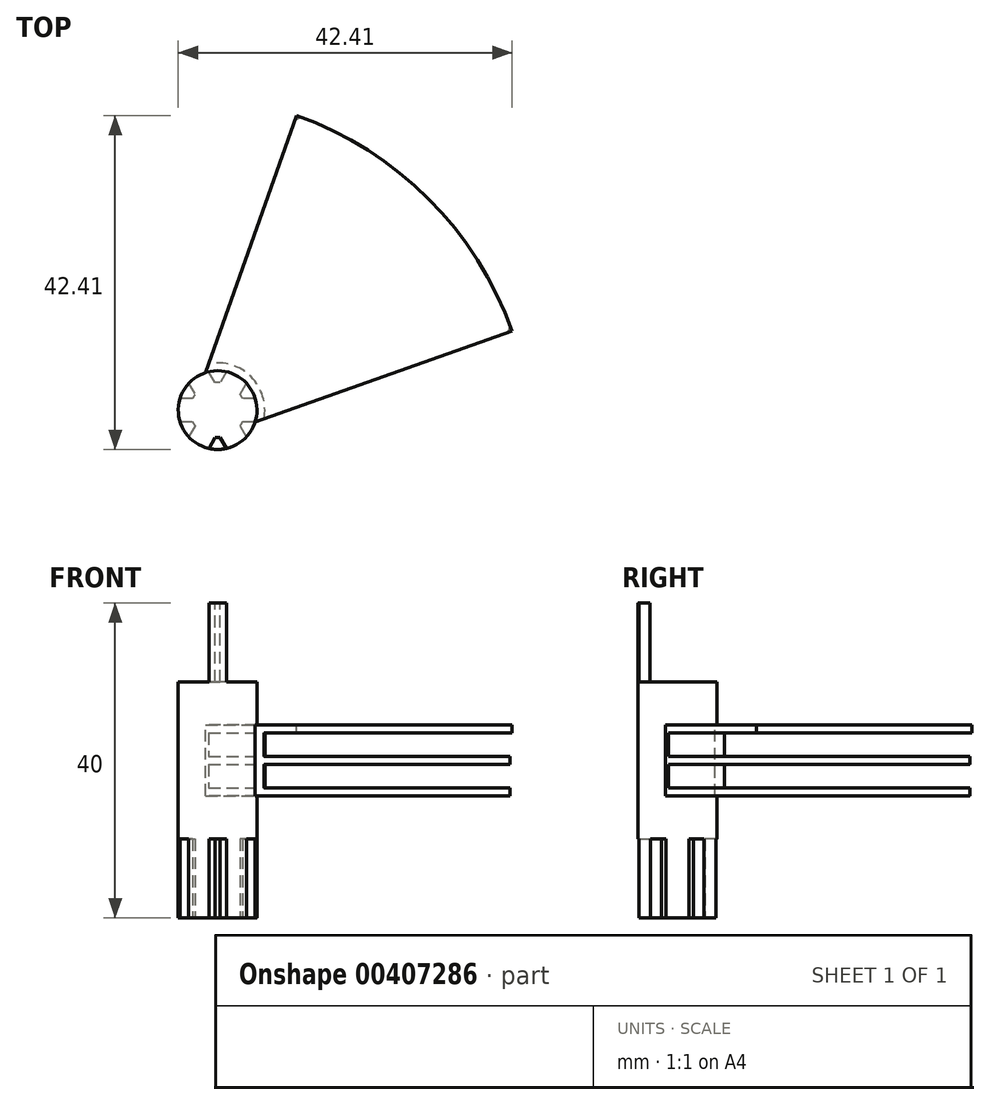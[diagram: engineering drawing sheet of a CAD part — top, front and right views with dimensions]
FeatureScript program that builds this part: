
annotation { "Feature Type Name" : "Feature", "Feature Type Description" : "" }
export const myFeature = defineFeature(function(context is Context, id is Id, definition is map)
    precondition{}
    {
        {
            var Q0;
            Q0=qCreatedBy(makeId("Top.planeOp"),FACE);
            var sketch = newSketch(context, id + "F0", { "sketchPlane" : qUnion([Q0])});
            skCircle(sketch, "E0", {"center": v(0, 0) * mm, "radius": 5 * mm});
            skSolve(sketch);
        }
        {
            var Q0;
            Q0 = qSketchRegion(id + "F0", true);
            extrude(context, id + "F1", {"entities" : qUnion([Q0]), "endBound" : BoundingType.SYMMETRIC, "depth" : 40 * mm});
        }
        {
            var Q0;
            Q0=qCreatedBy(makeId("Top.planeOp"),FACE);
            var sketch = newSketch(context, id + "F2", { "sketchPlane" : qUnion([Q0])});
            skCircle(sketch, "E1", {"center": v(0, 0) * mm, "radius": 40 * mm, "construction": true});
            skCircle(sketch, "E2.0", {"center": v(0, 0) * mm, "radius": 5 * mm});
            skLineSegment(sketch, "E3", {"start": v(0, 0) * mm, "end": v(-5, 0) * mm, "construction": true});
            skLineSegment(sketch, "E4", {"start": v(0, 0) * mm, "end": v(0, -5) * mm, "construction": true});
            skLineSegment(sketch, "E5", {"start": v(0, -5) * mm, "end": v(-6.33, -5) * mm, "construction": true});
            skLineSegment(sketch, "E6", {"start": v(-6.33, -5) * mm, "end": v(-6.33, 0) * mm, "construction": true});
            skLineSegment(sketch, "E7", {"start": v(-6.33, 0) * mm, "end": v(-5, 0) * mm, "construction": true});
            skLineSegment(sketch, "E8", {"start": v(-5, 0) * mm, "end": v(-5, -5) * mm, "construction": true});
            skCircle(sketch, "E9", {"center": v(-5, -5) * mm, "radius": 45 * mm});
            skSolve(sketch);
        }
        {
            var Q0;
            Q0=makeQuery(id+"F2.imprint","IMPRINT",FACE,{"disambiguationData":[TD([[makeQuery(id+"F2.imprint","IMPRINT",EDGE,{"derivedFrom":sQuery(id+"F2.wireOp",EDGE,"E2.0")}),-1.0]])]});
            extrude(context, id + "F3", {"entities" : qUnion([Q0]), "operationType" : NewBodyOperationType.ADD, "endBound" : BoundingType.SYMMETRIC, "depth" : 9 * mm});
        }
        {
            var Q0;
            Q0=qCreatedBy(makeId("Front.planeOp"),FACE);
            var sketch = newSketch(context, id + "F4", { "sketchPlane" : qUnion([Q0])});
            skLineSegment(sketch, "E10", {"start": v(47.5, 3.5) * mm, "end": v(6, 3.5) * mm});
            skLineSegment(sketch, "E11", {"start": v(47.5, 0.5) * mm, "end": v(6, 0.5) * mm});
            skLineSegment(sketch, "E12", {"start": v(47.5, -3.5) * mm, "end": v(6, -3.5) * mm});
            skPoint(sketch, "E13.orphan", {"position": v(-45, -4.5) * mm});
            skPoint(sketch, "E14.orphan", {"position": v(-45, 4.5) * mm});
            skLineSegment(sketch, "E15", {"start": v(47.5, 3.5) * mm, "end": v(47.5, 0.5) * mm});
            skLineSegment(sketch, "E16", {"start": v(47.5, -0.5) * mm, "end": v(47.5, -3.5) * mm});
            skLineSegment(sketch, "E17.trimOffspring", {"start": v(0, 4.5) * mm, "end": v(0, 22.27) * mm, "construction": true});
            skLineSegment(sketch, "E18.trimOffspring", {"start": v(0, -4.5) * mm, "end": v(0, -22.41) * mm, "construction": true});
            skLineSegment(sketch, "E19", {"start": v(-5, 4.5) * mm, "end": v(-5, 20) * mm, "construction": true});
            skLineSegment(sketch, "E20", {"start": v(5, 20) * mm, "end": v(5, 4.5) * mm, "construction": true});
            skLineSegment(sketch, "E21", {"start": v(-5, -20) * mm, "end": v(-5, -4.5) * mm, "construction": true});
            skLineSegment(sketch, "E22", {"start": v(5, -4.5) * mm, "end": v(5, -20) * mm, "construction": true});
            skLineSegment(sketch, "E23", {"start": v(5, 4.5) * mm, "end": v(5, 3.5) * mm, "construction": true});
            skLineSegment(sketch, "E24", {"start": v(47.5, -0.5) * mm, "end": v(6, -0.5) * mm});
            skLineSegment(sketch, "E25", {"start": v(6, -3.5) * mm, "end": v(6, -0.5) * mm});
            skLineSegment(sketch, "E26.trimOffspring", {"start": v(5, 0.5) * mm, "end": v(5, -0.5) * mm, "construction": true});
            skLineSegment(sketch, "E27.trimOffspring", {"start": v(6, 0.5) * mm, "end": v(6, 3.5) * mm});
            skLineSegment(sketch, "E28.trimOffspring", {"start": v(5, -3.5) * mm, "end": v(5, -4.5) * mm, "construction": true});
            skSolve(sketch);
        }
        {
            var Q0;
            Q0=makeQuery(id+"F4.imprint","IMPRINT",FACE,{"disambiguationData":[TD([[makeQuery(id+"F4.imprint","IMPRINT",EDGE,{"derivedFrom":sQuery(id+"F4.wireOp",EDGE,"E12")}),-1.0]])]});
            var Q1;
            Q1=makeQuery(id+"F4.imprint","IMPRINT",FACE,{"disambiguationData":[TD([[makeQuery(id+"F4.imprint","IMPRINT",EDGE,{"derivedFrom":sQuery(id+"F4.wireOp",EDGE,"E10")}),1.0]])]});
            var Q2;
            Q2=sQuery(id+"F4.wireOp",EDGE,"E18.trimOffspring");
            revolve(context, id + "F5", {"operationType" : NewBodyOperationType.REMOVE, "entities" : qUnion([Q0, Q1]), "axis" : qUnion([Q2]), "revolveType" : RevolveType.FULL, "oppositeDirection" : true});
        }
        {
            var Q0;
            Q0=makeQuery(id+"F1.opExtrude","CAP_FACE",FACE,{"disambiguationData":[OSD([sQuery(id+"F0.wireOp",EDGE,"E0")])],"isStart":false});
            var sketch = newSketch(context, id + "F6", { "sketchPlane" : qUnion([Q0])});
            skArc(sketch, "E29.0", {"start": v(-1.54, 4.76) * mm, "mid": v(-3.54, -3.54) * mm, "end": v(4.76, -1.54) * mm, "construction": true});
            skLineSegment(sketch, "E30", {"start": v(-5, -5) * mm, "end": v(-5, 35) * mm, "construction": true});
            skLineSegment(sketch, "E31", {"start": v(-5, -5) * mm, "end": v(35, -5) * mm, "construction": true});
            skLineSegment(sketch, "E32", {"start": v(-5, -5) * mm, "end": v(10.05, 37.4) * mm, "construction": true});
            skLineSegment(sketch, "E33", {"start": v(-0.79, 6.87) * mm, "end": v(10.05, 37.4) * mm});
            skArc(sketch, "E34", {"start": v(10.05, 37.4) * mm, "mid": v(-36.82, -36.82) * mm, "end": v(37.4, 10.05) * mm});
            skPoint(sketch, "E35.MirrorCS.end.orphan", {"position": v(23.28, 23.28) * mm});
            skPoint(sketch, "E35.MirrorCS.start.orphan", {"position": v(33.7, 17.96) * mm});
            skArc(sketch, "E36", {"start": v(-1.54, 4.76) * mm, "mid": v(-3.54, -3.54) * mm, "end": v(4.76, -1.54) * mm});
            skArc(sketch, "E37.trimOffspring", {"start": v(6.22, 1.25) * mm, "mid": v(3.98, 5.63) * mm, "end": v(-0.79, 6.87) * mm, "construction": true});
            skLineSegment(sketch, "E38", {"start": v(-1.54, 4.76) * mm, "end": v(-0.79, 6.87) * mm});
            skArc(sketch, "E39", {"start": v(26.82, 26.82) * mm, "mid": v(19.02, 33.05) * mm, "end": v(10.05, 37.4) * mm});
            skLineSegment(sketch, "E40", {"start": v(-5, -5) * mm, "end": v(26.82, 26.82) * mm, "construction": true});
            skArc(sketch, "E41", {"start": v(26.82, 26.82) * mm, "mid": v(33.05, 19.02) * mm, "end": v(37.4, 10.05) * mm});
            skLineSegment(sketch, "E42", {"start": v(-5, -5) * mm, "end": v(37.4, 10.05) * mm});
            skSolve(sketch);
        }
        {
            var Q0;
            Q0=makeQuery(id+"F6.imprint","IMPRINT",FACE,{"disambiguationData":[TD([[makeQuery(id+"F6.imprint","IMPRINT",EDGE,{"derivedFrom":sQuery(id+"F6.wireOp",EDGE,"E33")}),1.0]])]});
            extrude(context, id + "F7", {"entities" : qUnion([Q0]), "operationType" : NewBodyOperationType.REMOVE, "endBound" : BoundingType.THROUGH_ALL, "oppositeDirection" : true, "depth" : 25 * mm});
        }
        {
            var Q0;
            {var subQ1=sQuery(id+"F6.wireOp",EDGE,"E33");Q0=makeQuery(id+"F7.boolean.opBoolean","COPY",EDGE,{"disambiguationData":[TD([makeQuery(id+"F5.boolean.opBoolean","COPY",FACE,{"derivedFrom":makeQuery(id+"F5.opRevolve","SWEPT_FACE",FACE,{"disambiguationData":[OSD([sQuery(id+"F4.wireOp",EDGE,"E12")])]})})])],"derivedFrom":makeQuery(id+"F7.opExtrude","SWEPT_EDGE",EDGE,{"disambiguationData":[OSD([subQ1,sQuery(id+"F6.wireOp",EDGE,"E34")])]})});}
            var Q1;
            {var subQ0=sQuery(id+"F6.wireOp",EDGE,"E33");Q1=makeQuery(id+"F7.boolean.opBoolean","COPY",EDGE,{"disambiguationData":[TD([makeQuery(id+"F5.boolean.opBoolean","COPY",FACE,{"derivedFrom":makeQuery(id+"F5.opRevolve","SWEPT_FACE",FACE,{"disambiguationData":[OSD([sQuery(id+"F4.wireOp",EDGE,"E11")])]})})])],"derivedFrom":makeQuery(id+"F7.opExtrude","SWEPT_EDGE",EDGE,{"disambiguationData":[OSD([subQ0,sQuery(id+"F6.wireOp",EDGE,"E34")])]})});}
            var Q2;
            {var subQ1=sQuery(id+"F6.wireOp",EDGE,"E33");Q2=makeQuery(id+"F7.boolean.opBoolean","COPY",EDGE,{"disambiguationData":[TD([makeQuery(id+"F5.boolean.opBoolean","COPY",FACE,{"derivedFrom":makeQuery(id+"F5.opRevolve","SWEPT_FACE",FACE,{"disambiguationData":[OSD([sQuery(id+"F4.wireOp",EDGE,"E10")])]})})])],"derivedFrom":makeQuery(id+"F7.opExtrude","SWEPT_EDGE",EDGE,{"disambiguationData":[OSD([subQ1,sQuery(id+"F6.wireOp",EDGE,"E34")])]})});}
            var Q3;
            {var subQ1=sQuery(id+"F6.wireOp",EDGE,"bP0qAmGH-CtDD-ZhHH-eiUR-qPhmpkNQPwfo");Q3=makeQuery(id+"F7.boolean.opBoolean","COPY",EDGE,{"disambiguationData":[TD([makeQuery(id+"F5.boolean.opBoolean","COPY",FACE,{"derivedFrom":makeQuery(id+"F5.opRevolve","SWEPT_FACE",FACE,{"disambiguationData":[OSD([sQuery(id+"F4.wireOp",EDGE,"E12")])]})})])],"derivedFrom":makeQuery(id+"F7.opExtrude","SWEPT_EDGE",EDGE,{"disambiguationData":[OSD([subQ1,sQuery(id+"F6.wireOp",EDGE,"E34")])]})});}
            var Q4;
            {var subQ0=sQuery(id+"F6.wireOp",EDGE,"bP0qAmGH-CtDD-ZhHH-eiUR-qPhmpkNQPwfo");Q4=makeQuery(id+"F7.boolean.opBoolean","COPY",EDGE,{"disambiguationData":[TD([makeQuery(id+"F5.boolean.opBoolean","COPY",FACE,{"derivedFrom":makeQuery(id+"F5.opRevolve","SWEPT_FACE",FACE,{"disambiguationData":[OSD([sQuery(id+"F4.wireOp",EDGE,"E11")])]})})])],"derivedFrom":makeQuery(id+"F7.opExtrude","SWEPT_EDGE",EDGE,{"disambiguationData":[OSD([subQ0,sQuery(id+"F6.wireOp",EDGE,"E34")])]})});}
            var Q5;
            {var subQ1=sQuery(id+"F6.wireOp",EDGE,"bP0qAmGH-CtDD-ZhHH-eiUR-qPhmpkNQPwfo");Q5=makeQuery(id+"F7.boolean.opBoolean","COPY",EDGE,{"disambiguationData":[TD([makeQuery(id+"F5.boolean.opBoolean","COPY",FACE,{"derivedFrom":makeQuery(id+"F5.opRevolve","SWEPT_FACE",FACE,{"disambiguationData":[OSD([sQuery(id+"F4.wireOp",EDGE,"E10")])]})})])],"derivedFrom":makeQuery(id+"F7.opExtrude","SWEPT_EDGE",EDGE,{"disambiguationData":[OSD([subQ1,sQuery(id+"F6.wireOp",EDGE,"E34")])]})});}
            fillet(context, id + "F8", {"entities" : qUnion([Q0, Q1, Q2, Q3, Q4, Q5]), "radius" : 1 * mm, "tangentPropagation" : true, "allowEdgeOverflow" : false});
        }
        {
            var Q0;
            Q0=makeQuery(id+"F1.opExtrude","CAP_FACE",FACE,{"disambiguationData":[OSD([sQuery(id+"F0.wireOp",EDGE,"E0")])],"isStart":false});
            var sketch = newSketch(context, id + "F9", { "sketchPlane" : qUnion([Q0])});
            skCircle(sketch, "E43", {"center": v(0, 0) * mm, "radius": 3.5 * mm, "construction": true});
            skLineSegment(sketch, "E44", {"start": v(0, 0) * mm, "end": v(5, 0) * mm, "construction": true});
            skLineSegment(sketch, "E45", {"start": v(0, 0) * mm, "end": v(-5, 0) * mm, "construction": true});
            skLineSegment(sketch, "E46", {"start": v(0, 0) * mm, "end": v(-2.5, 4.33) * mm, "construction": true});
            skLineSegment(sketch, "E47", {"start": v(0, 0) * mm, "end": v(2.5, 4.33) * mm, "construction": true});
            skLineSegment(sketch, "E48", {"start": v(0, 0) * mm, "end": v(-2.5, -4.33) * mm, "construction": true});
            skLineSegment(sketch, "E49", {"start": v(0, 0) * mm, "end": v(2.5, -4.33) * mm, "construction": true});
            skArc(sketch, "E50", {"start": v(-2.5, 4.33) * mm, "mid": v(-1.82, 4.66) * mm, "end": v(-1.1, 4.88) * mm});
            skArc(sketch, "E51", {"start": v(-2.5, 4.33) * mm, "mid": v(-3.12, 3.9) * mm, "end": v(-3.67, 3.4) * mm});
            skArc(sketch, "E52", {"start": v(2.5, 4.33) * mm, "mid": v(1.82, 4.66) * mm, "end": v(1.1, 4.88) * mm});
            skArc(sketch, "E53", {"start": v(2.5, 4.33) * mm, "mid": v(3.12, 3.9) * mm, "end": v(3.67, 3.4) * mm});
            skArc(sketch, "E54", {"start": v(5, 0) * mm, "mid": v(4.94, 0.75) * mm, "end": v(4.78, 1.48) * mm});
            skArc(sketch, "E55", {"start": v(5, 0) * mm, "mid": v(4.94, -0.75) * mm, "end": v(4.78, -1.48) * mm});
            skArc(sketch, "E56", {"start": v(2.5, -4.33) * mm, "mid": v(1.82, -4.66) * mm, "end": v(1.1, -4.88) * mm});
            skArc(sketch, "E57", {"start": v(2.5, -4.33) * mm, "mid": v(3.12, -3.9) * mm, "end": v(3.67, -3.4) * mm});
            skArc(sketch, "E58", {"start": v(-2.5, -4.33) * mm, "mid": v(-1.82, -4.66) * mm, "end": v(-1.1, -4.88) * mm});
            skArc(sketch, "E59", {"start": v(-2.5, -4.33) * mm, "mid": v(-3.12, -3.9) * mm, "end": v(-3.67, -3.4) * mm});
            skArc(sketch, "E60", {"start": v(-5, 0) * mm, "mid": v(-4.94, -0.75) * mm, "end": v(-4.78, -1.48) * mm});
            skArc(sketch, "E61", {"start": v(-5, 0) * mm, "mid": v(-4.94, 0.75) * mm, "end": v(-4.78, 1.48) * mm});
            skLineSegment(sketch, "E62", {"start": v(-3.67, 3.4) * mm, "end": v(1.1, -4.88) * mm, "construction": true});
            skLineSegment(sketch, "E63", {"start": v(3.67, -3.4) * mm, "end": v(-1.1, 4.88) * mm, "construction": true});
            skLineSegment(sketch, "E64", {"start": v(1.1, 4.88) * mm, "end": v(-3.67, -3.4) * mm, "construction": true});
            skLineSegment(sketch, "E65", {"start": v(-1.1, -4.88) * mm, "end": v(3.67, 3.4) * mm, "construction": true});
            skLineSegment(sketch, "E66", {"start": v(4.78, 1.48) * mm, "end": v(-4.78, 1.48) * mm, "construction": true});
            skLineSegment(sketch, "E67", {"start": v(-4.78, -1.48) * mm, "end": v(4.78, -1.48) * mm, "construction": true});
            skArc(sketch, "E68", {"start": v(-2.87, 2) * mm, "mid": v(-3.03, 1.75) * mm, "end": v(-3.17, 1.48) * mm});
            skArc(sketch, "E69", {"start": v(-3.17, -1.48) * mm, "mid": v(-3.03, -1.75) * mm, "end": v(-2.87, -2) * mm});
            skArc(sketch, "E70", {"start": v(0.3, -3.49) * mm, "mid": v(0, -3.5) * mm, "end": v(-0.3, -3.49) * mm});
            skArc(sketch, "E71", {"start": v(2.87, -2) * mm, "mid": v(3.03, -1.75) * mm, "end": v(3.17, -1.48) * mm});
            skArc(sketch, "E72", {"start": v(3.17, 1.48) * mm, "mid": v(3.03, 1.75) * mm, "end": v(2.87, 2) * mm});
            skArc(sketch, "E73", {"start": v(0.3, 3.49) * mm, "mid": v(0, 3.5) * mm, "end": v(-0.3, 3.49) * mm});
            skLineSegment(sketch, "E74", {"start": v(-1.1, 4.88) * mm, "end": v(-0.3, 3.49) * mm});
            skLineSegment(sketch, "E75", {"start": v(0.3, 3.49) * mm, "end": v(1.1, 4.88) * mm});
            skLineSegment(sketch, "E76", {"start": v(2.87, 2) * mm, "end": v(3.67, 3.4) * mm});
            skLineSegment(sketch, "E77", {"start": v(3.17, 1.48) * mm, "end": v(4.78, 1.48) * mm});
            skLineSegment(sketch, "E78", {"start": v(4.78, -1.48) * mm, "end": v(3.17, -1.48) * mm});
            skLineSegment(sketch, "E79", {"start": v(3.67, -3.4) * mm, "end": v(2.87, -2) * mm});
            skLineSegment(sketch, "E80", {"start": v(1.1, -4.88) * mm, "end": v(0.3, -3.49) * mm});
            skLineSegment(sketch, "E81", {"start": v(-1.1, -4.88) * mm, "end": v(-0.3, -3.49) * mm});
            skLineSegment(sketch, "E82", {"start": v(-3.67, -3.4) * mm, "end": v(-2.87, -2) * mm});
            skLineSegment(sketch, "E83", {"start": v(-4.78, -1.48) * mm, "end": v(-3.17, -1.48) * mm});
            skLineSegment(sketch, "E84", {"start": v(-4.78, 1.48) * mm, "end": v(-3.17, 1.48) * mm});
            skLineSegment(sketch, "E85", {"start": v(-2.87, 2) * mm, "end": v(-3.67, 3.4) * mm});
            skSolve(sketch);
        }
        {
            var Q0;
            Q0=makeQuery(id+"F9.imprint","IMPRINT",FACE,{"disambiguationData":[TD([[makeQuery(id+"F9.imprint","IMPRINT",EDGE,{"derivedFrom":sQuery(id+"F9.wireOp",EDGE,"E68")}),-1.0]])]});
            var Q1;
            Q1=makeQuery(id+"F9.imprint","IMPRINT",FACE,{"disambiguationData":[TD([[makeQuery(id+"F9.imprint","IMPRINT",EDGE,{"derivedFrom":sQuery(id+"F9.wireOp",EDGE,"E73")}),-1.0]])]});
            var Q2;
            Q2=makeQuery(id+"F9.imprint","IMPRINT",FACE,{"disambiguationData":[TD([[makeQuery(id+"F9.imprint","IMPRINT",EDGE,{"derivedFrom":sQuery(id+"F9.wireOp",EDGE,"E72")}),-1.0]])]});
            var Q3;
            Q3=makeQuery(id+"F9.imprint","IMPRINT",FACE,{"disambiguationData":[TD([[makeQuery(id+"F9.imprint","IMPRINT",EDGE,{"derivedFrom":sQuery(id+"F9.wireOp",EDGE,"E71")}),-1.0]])]});
            var Q4;
            Q4=makeQuery(id+"F9.imprint","IMPRINT",FACE,{"disambiguationData":[TD([[makeQuery(id+"F9.imprint","IMPRINT",EDGE,{"derivedFrom":sQuery(id+"F9.wireOp",EDGE,"E70")}),1.0]])]});
            var Q5;
            Q5=makeQuery(id+"F9.imprint","IMPRINT",FACE,{"disambiguationData":[TD([[makeQuery(id+"F9.imprint","IMPRINT",EDGE,{"derivedFrom":sQuery(id+"F9.wireOp",EDGE,"E69")}),-1.0]])]});
            extrude(context, id + "F10", {"entities" : qUnion([Q0, Q1, Q2, Q3, Q4, Q5]), "operationType" : NewBodyOperationType.REMOVE, "oppositeDirection" : true, "depth" : 10 * mm});
        }
        {
            var Q0;
            Q0=makeQuery(id+"F1.opExtrude","CAP_FACE",FACE,{"disambiguationData":[OSD([sQuery(id+"F0.wireOp",EDGE,"E0")])],"isStart":true});
            var sketch = newSketch(context, id + "F11", { "sketchPlane" : qUnion([Q0])});
            skLineSegment(sketch, "E86.0.0", {"start": v(1.1, -4.88) * mm, "end": v(0.3, -3.49) * mm});
            skArc(sketch, "E86.0.1", {"start": v(0.3, -3.49) * mm, "mid": v(0, -3.5) * mm, "end": v(-0.3, -3.49) * mm});
            skLineSegment(sketch, "E86.0.2", {"start": v(-0.3, -3.49) * mm, "end": v(-1.1, -4.88) * mm});
            skArc(sketch, "E86.0.3", {"start": v(-1.1, -4.88) * mm, "mid": v(-2.5, -4.33) * mm, "end": v(-3.67, -3.4) * mm});
            skLineSegment(sketch, "E86.0.4", {"start": v(-3.67, -3.4) * mm, "end": v(-2.87, -2) * mm});
            skArc(sketch, "E86.0.5", {"start": v(-2.87, -2) * mm, "mid": v(-3.03, -1.75) * mm, "end": v(-3.17, -1.48) * mm});
            skLineSegment(sketch, "E86.0.6", {"start": v(-3.17, -1.48) * mm, "end": v(-4.78, -1.48) * mm});
            skArc(sketch, "E86.0.7", {"start": v(-4.78, -1.48) * mm, "mid": v(-5, 0) * mm, "end": v(-4.78, 1.48) * mm});
            skLineSegment(sketch, "E86.0.8", {"start": v(-4.78, 1.48) * mm, "end": v(-3.17, 1.48) * mm});
            skArc(sketch, "E86.0.9", {"start": v(-3.17, 1.48) * mm, "mid": v(-3.03, 1.75) * mm, "end": v(-2.87, 2) * mm});
            skLineSegment(sketch, "E86.0.10", {"start": v(-2.87, 2) * mm, "end": v(-3.67, 3.4) * mm});
            skArc(sketch, "E86.0.11", {"start": v(-3.67, 3.4) * mm, "mid": v(-2.5, 4.33) * mm, "end": v(-1.1, 4.88) * mm});
            skLineSegment(sketch, "E86.0.12", {"start": v(-1.1, 4.88) * mm, "end": v(-0.3, 3.49) * mm});
            skArc(sketch, "E86.0.13", {"start": v(-0.3, 3.49) * mm, "mid": v(0, 3.5) * mm, "end": v(0.3, 3.49) * mm});
            skLineSegment(sketch, "E86.0.14", {"start": v(0.3, 3.49) * mm, "end": v(1.1, 4.88) * mm});
            skArc(sketch, "E86.0.15", {"start": v(1.1, 4.88) * mm, "mid": v(2.5, 4.33) * mm, "end": v(3.67, 3.4) * mm});
            skLineSegment(sketch, "E86.0.16", {"start": v(3.67, 3.4) * mm, "end": v(2.87, 2) * mm});
            skArc(sketch, "E86.0.17", {"start": v(2.87, 2) * mm, "mid": v(3.03, 1.75) * mm, "end": v(3.17, 1.48) * mm});
            skLineSegment(sketch, "E86.0.18", {"start": v(3.17, 1.48) * mm, "end": v(4.78, 1.48) * mm});
            skArc(sketch, "E86.0.19", {"start": v(4.78, 1.48) * mm, "mid": v(5, 0) * mm, "end": v(4.78, -1.48) * mm});
            skLineSegment(sketch, "E86.0.20", {"start": v(4.78, -1.48) * mm, "end": v(3.17, -1.48) * mm});
            skArc(sketch, "E86.0.21", {"start": v(3.17, -1.48) * mm, "mid": v(3.03, -1.75) * mm, "end": v(2.87, -2) * mm});
            skLineSegment(sketch, "E86.0.22", {"start": v(2.87, -2) * mm, "end": v(3.67, -3.4) * mm});
            skArc(sketch, "E86.0.23", {"start": v(3.67, -3.4) * mm, "mid": v(2.5, -4.33) * mm, "end": v(1.1, -4.88) * mm});
            skSolve(sketch);
        }
        {
            var Q0;
            {var subQ0=sQuery(id+"F11.wireOp",EDGE,"E86.0.12");Q0=makeQuery(id+"F11.imprint","IMPRINT",FACE,{"disambiguationData":[TD([[makeQuery(id+"F11.imprint","IMPRINT",EDGE,{"derivedFrom":subQ0}),1.0]])]});}
            var Q1;
            {var subQ0=sQuery(id+"F11.wireOp",EDGE,"E86.0.16");Q1=makeQuery(id+"F11.imprint","IMPRINT",FACE,{"disambiguationData":[TD([[makeQuery(id+"F11.imprint","IMPRINT",EDGE,{"derivedFrom":subQ0}),1.0]])]});}
            var Q2;
            {var subQ0=sQuery(id+"F11.wireOp",EDGE,"E86.0.20");Q2=makeQuery(id+"F11.imprint","IMPRINT",FACE,{"disambiguationData":[TD([[makeQuery(id+"F11.imprint","IMPRINT",EDGE,{"derivedFrom":subQ0}),1.0]])]});}
            var Q3;
            {var subQ0=sQuery(id+"F11.wireOp",EDGE,"E86.0.0");Q3=makeQuery(id+"F11.imprint","IMPRINT",FACE,{"disambiguationData":[TD([[makeQuery(id+"F11.imprint","IMPRINT",EDGE,{"derivedFrom":subQ0}),1.0]])]});}
            var Q4;
            {var subQ0=sQuery(id+"F11.wireOp",EDGE,"E86.0.4");Q4=makeQuery(id+"F11.imprint","IMPRINT",FACE,{"disambiguationData":[TD([[makeQuery(id+"F11.imprint","IMPRINT",EDGE,{"derivedFrom":subQ0}),1.0]])]});}
            var Q5;
            {var subQ0=sQuery(id+"F11.wireOp",EDGE,"E86.0.8");Q5=makeQuery(id+"F11.imprint","IMPRINT",FACE,{"disambiguationData":[TD([[makeQuery(id+"F11.imprint","IMPRINT",EDGE,{"derivedFrom":subQ0}),1.0]])]});}
            extrude(context, id + "F12", {"entities" : qUnion([Q0, Q1, Q2, Q3, Q4, Q5]), "operationType" : NewBodyOperationType.REMOVE, "oppositeDirection" : true, "depth" : 10 * mm});
        }
    });
